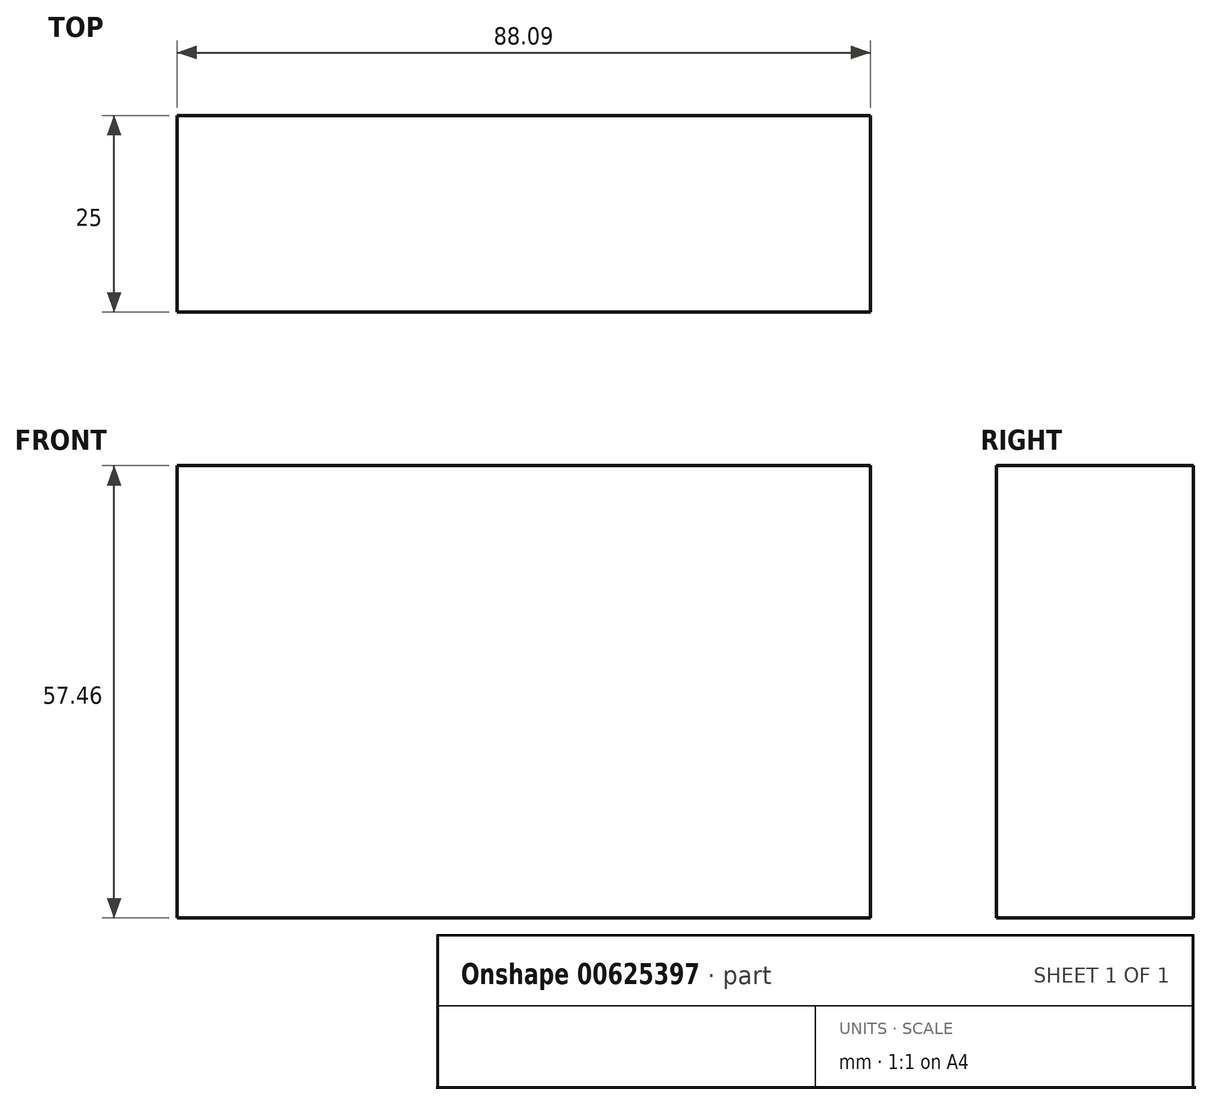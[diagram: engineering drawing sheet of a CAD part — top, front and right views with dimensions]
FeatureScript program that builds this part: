
annotation { "Feature Type Name" : "Feature", "Feature Type Description" : "" }
export const myFeature = defineFeature(function(context is Context, id is Id, definition is map)
    precondition{}
    {
        {
            var Q0;
            Q0=qCreatedBy(makeId("Front.planeOp"),FACE);
            var sketch = newSketch(context, id + "F0", { "sketchPlane" : qUnion([Q0])});
            skLineSegment(sketch, "E0.bottom", {"start": v(-48.4, 29.8) * mm, "end": v(39.69, 29.8) * mm});
            skLineSegment(sketch, "E0.top", {"start": v(-48.4, -27.67) * mm, "end": v(39.69, -27.67) * mm});
            skLineSegment(sketch, "E0.left", {"start": v(-48.4, 29.8) * mm, "end": v(-48.4, -27.67) * mm});
            skLineSegment(sketch, "E0.right", {"start": v(39.69, 29.8) * mm, "end": v(39.69, -27.67) * mm});
            skSolve(sketch);
        }
        {
            var Q0;
            Q0=makeQuery(id+"F0.imprint","IMPRINT",FACE,{"disambiguationData":[TD([[makeQuery(id+"F0.imprint","IMPRINT",EDGE,{"derivedFrom":sQuery(id+"F0.wireOp",EDGE,"E0.bottom")}),-1.0]])]});
            extrude(context, id + "F1", {"entities" : qUnion([Q0]), "oppositeDirection" : true, "depth" : 25 * mm, "offsetDistance" : 25 * mm});
        }
    });
